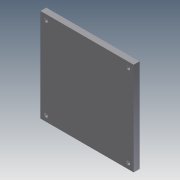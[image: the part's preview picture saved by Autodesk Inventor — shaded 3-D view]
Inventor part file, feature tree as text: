
AUTODESK INVENTOR PART (.ipt)
format: ipt  version: 2011 (Build 150239000, 239)  size: 162,816 bytes
history: native  units: in
note: dims shown in document units (in); Inventor stores cm internally (conversion verified against a paired STEP export)
features: extrude x10, sketch x10, fillet x1
ambient origin geometry x8: Origin, YZ Plane, XZ Plane, XY Plane, X Axis, Y Axis, Z Axis, Center Point
bodies: Solid1 (feature_tree)
feature tree (21):
  extrude  "Extrusion1"  Depth=4.0in
  extrude  "Extrusion2"  Depth=2.16in
  extrude  "Extrusion3"  Depth=1.7655in
  extrude  "Extrusion4"  Depth=0.029in TaperAngle=0.0deg
  extrude  "Extrusion5"  Depth=2.36in
  fillet  "Fillet1"  Radius=2.56in
  extrude  "Extrusion6"  Depth=0.125in
  extrude  "Extrusion7"  Depth=0.25in TaperAngle=0.0deg
  extrude  "Extrusion8"  Depth=0.25in
  extrude  "Extrusion9"  Depth=1.0in TaperAngle=0.0deg
  extrude  "Extrusion10"  Depth=0.25in TaperAngle=0.0deg
  sketch  "Sketch1"  dims[d0=4.0in d1=4.0in]
  sketch  "Sketch2"  dims[d2=0.029in d3=0.0in d4=2.16in]
  sketch  "Sketch3"  dims[d5=0.029in d6=0.0in d7=1.7655in]
  sketch  "Sketch4"  dims[d8=0.156in d9=0.029in d10=0.0in]
  sketch  "Sketch5"  dims[d11=0.029in d12=0.0in d13=2.36in d14=2.56in]
  sketch  "Sketch6"  dims[d15=0.262in d16=0.0in d17=0.125in]
  sketch  "Sketch7"  dims[d18=0.25in d19=0.0in d20=0.25in d21=0.0in]
  sketch  "Sketch8"  dims[d22=0.25in d23=0.25in]
  sketch  "Sketch9"  dims[d24=0.5in d25=1.0in d26=0.0in]
  sketch  "Sketch10"  dims[d27=1.0in d28=0.0in d29=0.25in d30=0.0in]
